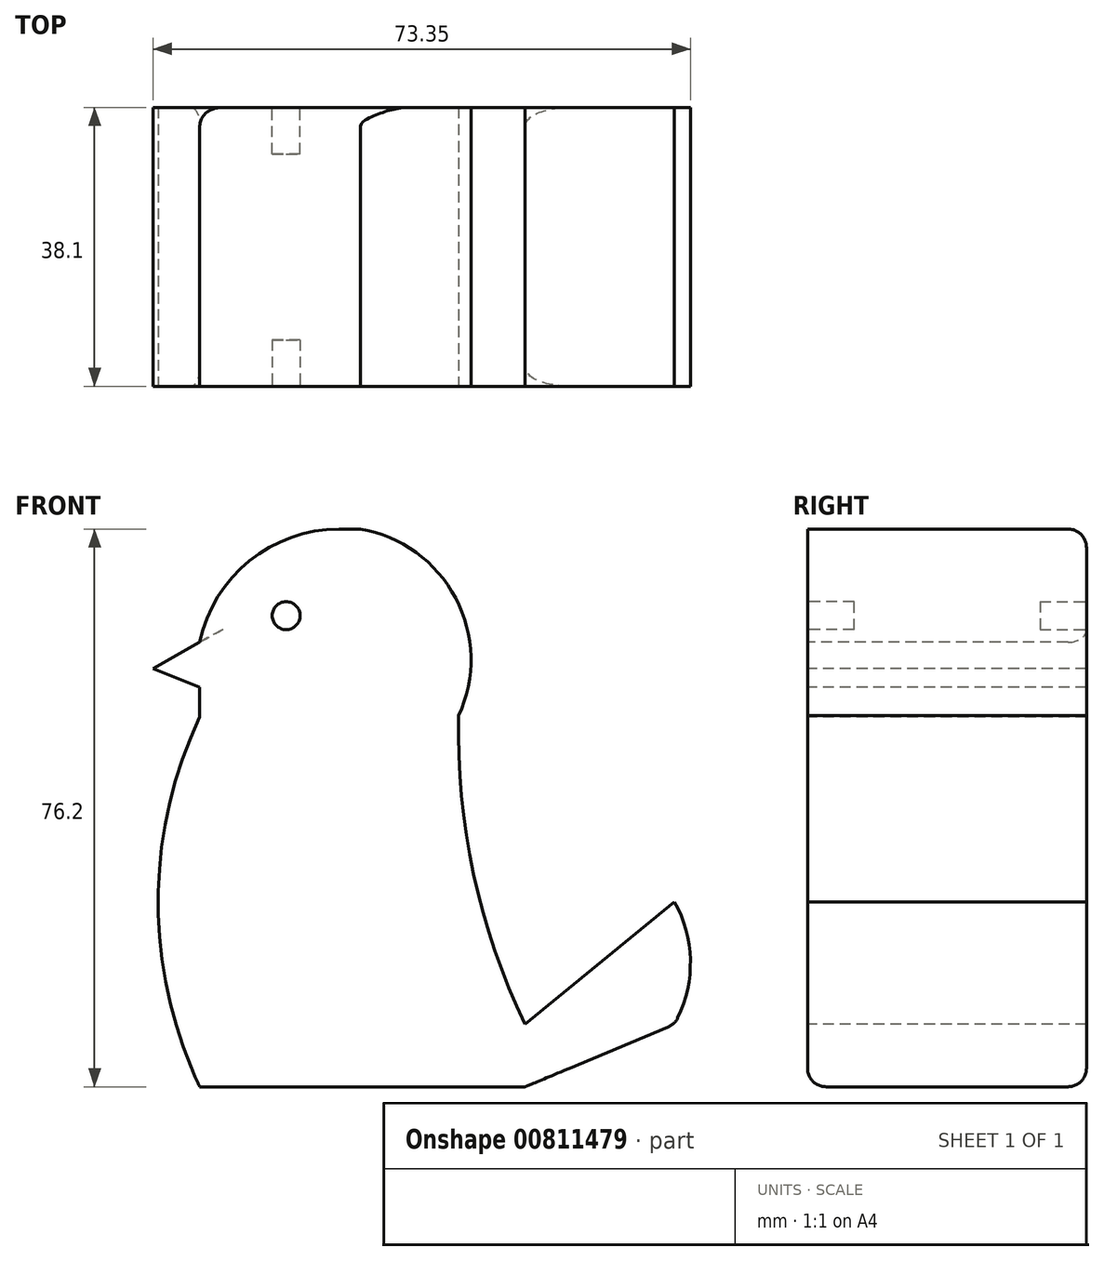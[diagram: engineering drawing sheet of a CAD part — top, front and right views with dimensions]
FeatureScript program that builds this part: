
annotation { "Feature Type Name" : "Feature", "Feature Type Description" : "" }
export const myFeature = defineFeature(function(context is Context, id is Id, definition is map)
    precondition{}
    {
        {
            var Q0;
            Q0=qCreatedBy(makeId("Front.planeOp"),FACE);
            var sketch = newSketch(context, id + "F0", { "sketchPlane" : qUnion([Q0])});
            skLineSegment(sketch, "E0", {"start": v(0, 0) * mm, "end": v(76.2, 0) * mm});
            skLineSegment(sketch, "E1", {"start": v(76.2, 0) * mm, "end": v(76.2, 76.2) * mm});
            skLineSegment(sketch, "E2", {"start": v(0, 76.2) * mm, "end": v(0, 0) * mm});
            skLineSegment(sketch, "E3", {"start": v(0, 76.2) * mm, "end": v(76.2, 76.2) * mm});
            skSolve(sketch);
        }
        {
            var Q0;
            Q0=makeQuery(id+"F0.imprint","IMPRINT",FACE,{"disambiguationData":[TD([[makeQuery(id+"F0.imprint","IMPRINT",EDGE,{"derivedFrom":sQuery(id+"F0.wireOp",EDGE,"E0")}),1.0]])]});
            extrude(context, id + "F1", {"entities" : qUnion([Q0]), "depth" : 38.1 * mm, "offsetDistance" : 25.4 * mm});
        }
        {
            var Q0;
            Q0=makeQuery(id+"F1.opExtrude","CAP_FACE",FACE,{"disambiguationData":[OSD([sQuery(id+"F0.wireOp",EDGE,"E0"),sQuery(id+"F0.wireOp",EDGE,"E1"),sQuery(id+"F0.wireOp",EDGE,"E2"),sQuery(id+"F0.wireOp",EDGE,"E3")])],"isStart":false});
            var sketch = newSketch(context, id + "F2", { "sketchPlane" : qUnion([Q0])});
            skLineSegment(sketch, "E4", {"start": v(0, 0) * mm, "end": v(6.35, 0) * mm, "construction": true});
            skLineSegment(sketch, "E5", {"start": v(6.35, 0) * mm, "end": v(6.35, 76.2) * mm, "construction": true});
            skLineSegment(sketch, "E6", {"start": v(0, 76.2) * mm, "end": v(0, 50.5) * mm, "construction": true});
            skLineSegment(sketch, "E7", {"start": v(0, 76.2) * mm, "end": v(0, 57.15) * mm, "construction": true});
            skLineSegment(sketch, "E8", {"start": v(0, 50.5) * mm, "end": v(6.35, 50.5) * mm, "construction": true});
            skArc(sketch, "E9", {"start": v(6.35, 50.5) * mm, "mid": v(0.66, 25.25) * mm, "end": v(6.35, 0) * mm});
            skLineSegment(sketch, "E10", {"start": v(6.35, 54.58) * mm, "end": v(0, 57.15) * mm});
            skLineSegment(sketch, "E11", {"start": v(0, 57.15) * mm, "end": v(6.35, 60.72) * mm});
            skLineSegment(sketch, "E12", {"start": v(6.35, 50.5) * mm, "end": v(6.35, 54.58) * mm});
            skLineSegment(sketch, "E13", {"start": v(0, 76.2) * mm, "end": v(19.05, 76.2) * mm, "construction": true});
            skLineSegment(sketch, "E14", {"start": v(0, 76.2) * mm, "end": v(25.4, 76.2) * mm, "construction": true});
            skArc(sketch, "E15", {"start": v(25.4, 76.2) * mm, "mid": v(13.13, 71.84) * mm, "end": v(6.35, 60.72) * mm});
            skLineSegment(sketch, "E16", {"start": v(0, 0) * mm, "end": v(0.66, 26) * mm, "construction": true});
            skPoint(sketch, "E16.endSnap0", {"position": v(0.66, 25.25) * mm});
            skLineSegment(sketch, "E17", {"start": v(0, 0) * mm, "end": v(0, 19.05) * mm, "construction": true});
            skLineSegment(sketch, "E18", {"start": v(0, 19.05) * mm, "end": v(76.2, 19.05) * mm, "construction": true});
            skSolve(sketch);
        }
        {
            var Q0;
            {var subQ0=sQuery(id+"F2.wireOp",EDGE,"E9");Q0=makeQuery(id+"F2.imprint","IMPRINT",FACE,{"disambiguationData":[TD([[makeQuery(id+"F2.imprint","IMPRINT",EDGE,{"derivedFrom":subQ0}),1.0]])]});}
            var sketch = newSketch(context, id + "F3", { "sketchPlane" : qUnion([Q0])});
            skLineSegment(sketch, "E19", {"start": v(0, 0) * mm, "end": v(50.8, 0) * mm, "construction": true});
            skLineSegment(sketch, "E20", {"start": v(50.8, 0) * mm, "end": v(71.17, 8.53) * mm, "construction": true});
            skLineSegment(sketch, "E21", {"start": v(71.17, 25.27) * mm, "end": v(50.8, 8.53) * mm, "construction": true});
            skArc(sketch, "E22", {"start": v(71.17, 8.53) * mm, "mid": v(73.35, 16.9) * mm, "end": v(71.17, 25.27) * mm});
            skLineSegment(sketch, "E23", {"start": v(6.05, 50.7) * mm, "end": v(77.37, 50.7) * mm, "construction": true});
            skArc(sketch, "E24", {"start": v(41.71, 50.7) * mm, "mid": v(40.7, 67.81) * mm, "end": v(25.9, 76.44) * mm});
            skArc(sketch, "E25", {"start": v(41.71, 50.7) * mm, "mid": v(43.74, 29.07) * mm, "end": v(50.8, 8.53) * mm});
            skLineSegment(sketch, "E26", {"start": v(64.72, 19.97) * mm, "end": v(71.17, 25.27) * mm});
            skLineSegment(sketch, "E27", {"start": v(71.17, 25.27) * mm, "end": v(50.8, 8.53) * mm});
            skLineSegment(sketch, "E28", {"start": v(50.8, 0) * mm, "end": v(71.17, 8.53) * mm});
            skSolve(sketch);
        }
        {
            var Q0;
            {var subQ3=sQuery(id+"F2.wireOp",EDGE,"E9");Q0=makeQuery(id+"F2.imprint","IMPRINT",FACE,{"disambiguationData":[TD([[makeQuery(id+"F2.imprint","IMPRINT",EDGE,{"derivedFrom":subQ3}),-1.0]])]});}
            var Q1;
            {var subQ0=sQuery(id+"F2.wireOp",EDGE,"E11");Q1=makeQuery(id+"F2.imprint","IMPRINT",FACE,{"disambiguationData":[TD([[makeQuery(id+"F2.imprint","IMPRINT",EDGE,{"derivedFrom":subQ0}),1.0]])]});}
            var Q2;
            {var subQ1=sQuery(id+"F3.wireOp",EDGE,"E22");Q2=makeQuery(id+"F3.imprint","IMPRINT",FACE,{"disambiguationData":[TD([[makeQuery(id+"F3.imprint","IMPRINT",EDGE,{"derivedFrom":subQ1}),-1.0]])]});}
            extrude(context, id + "F4", {"entities" : qUnion([Q0, Q1, Q2]), "operationType" : NewBodyOperationType.REMOVE, "endBound" : BoundingType.UP_TO_NEXT, "oppositeDirection" : true, "depth" : 25.4 * mm, "offsetDistance" : 25.4 * mm});
        }
        {
            var Q0;
            Q0=makeQuery(id+"F4.boolean.opBoolean","COPY",EDGE,{"derivedFrom":makeQuery(id+"F4.opExtrude","CAP_EDGE",EDGE,{"disambiguationData":[OSD([sQuery(id+"F2.wireOp",EDGE,"E9")])],"isStart":true})});
            var Q1;
            Q1=makeQuery(id+"F4.boolean.opBoolean","COPY",EDGE,{"derivedFrom":makeQuery(id+"F4.opExtrude","CAP_EDGE",EDGE,{"disambiguationData":[OSD([sQuery(id+"F2.wireOp",EDGE,"E15")])],"isStart":true})});
            var Q2;
            Q2=makeQuery(id+"F4.boolean.opBoolean","COPY",EDGE,{"derivedFrom":makeQuery(id+"F4.opExtrude","CAP_EDGE",EDGE,{"disambiguationData":[OSD([sQuery(id+"F2.wireOp",EDGE,"E11")])],"isStart":true})});
            var Q3;
            Q3=makeQuery(id+"F4.boolean.opBoolean","COPY",EDGE,{"derivedFrom":makeQuery(id+"F4.opExtrude","CAP_EDGE",EDGE,{"disambiguationData":[OSD([sQuery(id+"F2.wireOp",EDGE,"E10")])],"isStart":true})});
            var Q4;
            Q4=makeQuery(id+"F4.boolean.opBoolean","COPY",EDGE,{"derivedFrom":makeQuery(id+"F4.opExtrude","CAP_EDGE",EDGE,{"disambiguationData":[OSD([sQuery(id+"F2.wireOp",EDGE,"E12")])],"isStart":true})});
            var Q5;
            Q5=makeQuery(id+"F4.boolean.opBoolean","COPY",EDGE,{"derivedFrom":makeQuery(id+"F4.opExtrude","CAP_EDGE",EDGE,{"disambiguationData":[OSD([sQuery(id+"F3.wireOp",EDGE,"E25")])],"isStart":true})});
            var Q6;
            Q6=makeQuery(id+"F4.boolean.opBoolean","COPY",EDGE,{"derivedFrom":makeQuery(id+"F4.opExtrude","CAP_EDGE",EDGE,{"disambiguationData":[OSD([sQuery(id+"F3.wireOp",EDGE,"E24")])],"isStart":true})});
            var Q7;
            Q7=makeQuery(id+"F4.boolean.opBoolean","COPY",EDGE,{"derivedFrom":makeQuery(id+"F4.opExtrude","CAP_EDGE",EDGE,{"disambiguationData":[OSD([sQuery(id+"F3.wireOp",EDGE,"E27")])],"isStart":true})});
            var Q8;
            Q8=makeQuery(id+"F4.boolean.opBoolean","COPY",EDGE,{"derivedFrom":makeQuery(id+"F4.opExtrude","CAP_EDGE",EDGE,{"disambiguationData":[OSD([sQuery(id+"F3.wireOp",EDGE,"E22")])],"isStart":true})});
            var Q9;
            Q9=makeQuery(id+"F4.boolean.opBoolean","COPY",EDGE,{"derivedFrom":makeQuery(id+"F4.opExtrude","CAP_EDGE",EDGE,{"disambiguationData":[OSD([sQuery(id+"F3.wireOp",EDGE,"E28")])],"isStart":true})});
            var Q10;
            Q10=makeQuery(id+"F1.opExtrude","CAP_EDGE",EDGE,{"disambiguationData":[OSD([sQuery(id+"F0.wireOp",EDGE,"E0")])],"isStart":false});
            var Q11;
            Q11=makeQuery(id+"F4.boolean.opBoolean","COPY",EDGE,{"derivedFrom":makeQuery(id+"F4.opExtrude","CAP_EDGE",EDGE,{"disambiguationData":[OSD([sQuery(id+"F3.wireOp",EDGE,"E22")])],"isStart":false})});
            var Q12;
            Q12=makeQuery(id+"F4.boolean.opBoolean","COPY",EDGE,{"derivedFrom":makeQuery(id+"F4.opExtrude","CAP_EDGE",EDGE,{"disambiguationData":[OSD([sQuery(id+"F3.wireOp",EDGE,"E28")])],"isStart":false})});
            var Q13;
            Q13=makeQuery(id+"F4.boolean.opBoolean","COPY",EDGE,{"derivedFrom":makeQuery(id+"F4.opExtrude","CAP_EDGE",EDGE,{"disambiguationData":[OSD([sQuery(id+"F3.wireOp",EDGE,"E27")])],"isStart":false})});
            var Q14;
            Q14=makeQuery(id+"F4.boolean.opBoolean","COPY",EDGE,{"derivedFrom":makeQuery(id+"F4.opExtrude","CAP_EDGE",EDGE,{"disambiguationData":[OSD([sQuery(id+"F3.wireOp",EDGE,"E25")])],"isStart":false})});
            var Q15;
            Q15=makeQuery(id+"F1.opExtrude","CAP_EDGE",EDGE,{"disambiguationData":[OSD([sQuery(id+"F0.wireOp",EDGE,"E0")])],"isStart":true});
            var Q16;
            Q16=makeQuery(id+"F4.boolean.opBoolean","COPY",EDGE,{"derivedFrom":makeQuery(id+"F4.opExtrude","CAP_EDGE",EDGE,{"disambiguationData":[OSD([sQuery(id+"F2.wireOp",EDGE,"E9")])],"isStart":false})});
            var Q17;
            Q17=makeQuery(id+"F4.boolean.opBoolean","COPY",EDGE,{"derivedFrom":makeQuery(id+"F4.opExtrude","CAP_EDGE",EDGE,{"disambiguationData":[OSD([sQuery(id+"F2.wireOp",EDGE,"E12")])],"isStart":false})});
            var Q18;
            Q18=makeQuery(id+"F4.boolean.opBoolean","COPY",EDGE,{"derivedFrom":makeQuery(id+"F4.opExtrude","CAP_EDGE",EDGE,{"disambiguationData":[OSD([sQuery(id+"F2.wireOp",EDGE,"E10")])],"isStart":false})});
            var Q19;
            Q19=makeQuery(id+"F4.boolean.opBoolean","COPY",EDGE,{"derivedFrom":makeQuery(id+"F4.opExtrude","CAP_EDGE",EDGE,{"disambiguationData":[OSD([sQuery(id+"F2.wireOp",EDGE,"E11")])],"isStart":false})});
            var Q20;
            Q20=makeQuery(id+"F4.boolean.opBoolean","COPY",EDGE,{"derivedFrom":makeQuery(id+"F4.opExtrude","CAP_EDGE",EDGE,{"disambiguationData":[OSD([sQuery(id+"F2.wireOp",EDGE,"E15")])],"isStart":false})});
            var Q21;
            Q21=makeQuery(id+"F1.opExtrude","CAP_EDGE",EDGE,{"disambiguationData":[OSD([sQuery(id+"F0.wireOp",EDGE,"E3")])],"isStart":true});
            var Q22;
            Q22=makeQuery(id+"F4.boolean.opBoolean","COPY",EDGE,{"derivedFrom":makeQuery(id+"F4.opExtrude","CAP_EDGE",EDGE,{"disambiguationData":[OSD([sQuery(id+"F3.wireOp",EDGE,"E24")])],"isStart":false})});
            var Q23;
            Q23=makeQuery(id+"F4.boolean.opBoolean","COPY",EDGE,{"derivedFrom":makeQuery(id+"F4.opExtrude","SWEPT_EDGE",EDGE,{"disambiguationData":[OSD([sQuery(id+"F0.wireOp",EDGE,"E0"),sQuery(id+"F2.wireOp",EDGE,"E9")])]})});
            var Q24;
            Q24=makeQuery(id+"F4.boolean.opBoolean","COPY",EDGE,{"derivedFrom":makeQuery(id+"F4.opExtrude","SWEPT_EDGE",EDGE,{"disambiguationData":[OSD([sQuery(id+"F3.wireOp",EDGE,"E22"),sQuery(id+"F3.wireOp",EDGE,"E28")])]})});
            var Q25;
            Q25=makeQuery(id+"F4.boolean.opBoolean","COPY",EDGE,{"derivedFrom":makeQuery(id+"F4.opExtrude","SWEPT_EDGE",EDGE,{"disambiguationData":[OSD([sQuery(id+"F0.wireOp",EDGE,"E0"),sQuery(id+"F3.wireOp",EDGE,"E28")])]})});
            fillet(context, id + "F5", {"entities" : qUnion([Q0, Q1, Q2, Q3, Q4, Q5, Q6, Q7, Q8, Q9, Q10, Q11, Q12, Q13, Q14, Q15, Q16, Q17, Q18, Q19, Q20, Q21, Q22, Q23, Q24, Q25]), "radius" : 2.54 * mm, "tangentPropagation" : true, "allowEdgeOverflow" : false});
        }
        {
            var Q0;
            Q0=makeQuery(id+"F1.opExtrude","CAP_FACE",FACE,{"disambiguationData":[OSD([sQuery(id+"F0.wireOp",EDGE,"E0"),sQuery(id+"F0.wireOp",EDGE,"E1"),sQuery(id+"F0.wireOp",EDGE,"E2"),sQuery(id+"F0.wireOp",EDGE,"E3")])],"isStart":false});
            var sketch = newSketch(context, id + "F6", { "sketchPlane" : qUnion([Q0])});
            skLineSegment(sketch, "E29", {"start": v(10.3, 64.36) * mm, "end": v(40.79, 64.36) * mm, "construction": true});
            skCircle(sketch, "E30", {"center": v(18.15, 64.36) * mm, "radius": 1.9 * mm});
            skSolve(sketch);
        }
        {
            var Q0;
            Q0=makeQuery(id+"F6.imprint","IMPRINT",FACE,{"disambiguationData":[TD([[makeQuery(id+"F6.imprint","IMPRINT",EDGE,{"derivedFrom":sQuery(id+"F6.wireOp",EDGE,"E30")}),1.0]])]});
            var Q1;
            Q1=sQuery(id+"F6.wireOp",EDGE,"E30");
            extrude(context, id + "F7", {"entities" : qUnion([Q0]), "operationType" : NewBodyOperationType.REMOVE, "surfaceEntities" : qUnion([Q1]), "oppositeDirection" : true, "depth" : 6.35 * mm, "offsetDistance" : 25.4 * mm});
        }
        {
            var Q0;
            Q0=makeQuery(id+"F1.opExtrude","CAP_FACE",FACE,{"disambiguationData":[OSD([sQuery(id+"F0.wireOp",EDGE,"E0"),sQuery(id+"F0.wireOp",EDGE,"E1"),sQuery(id+"F0.wireOp",EDGE,"E2"),sQuery(id+"F0.wireOp",EDGE,"E3")])],"isStart":true});
            var sketch = newSketch(context, id + "F8", { "sketchPlane" : qUnion([Q0])});
            skSolve(sketch);
        }
        {
            var Q0;
            Q0=makeQuery(id+"F6.imprint","IMPRINT",FACE,{"disambiguationData":[TD([[makeQuery(id+"F6.imprint","IMPRINT",EDGE,{"derivedFrom":sQuery(id+"F6.wireOp",EDGE,"E30")}),1.0]])]});
            extrude(context, id + "F9", {"entities" : qUnion([Q0]), "operationType" : NewBodyOperationType.REMOVE, "oppositeDirection" : true, "depth" : 6.35 * mm, "offsetDistance" : 25.4 * mm});
        }
        {
            var Q0;
            {var subQ0=sQuery(id+"F0.wireOp",EDGE,"E3");var subQ1=sQuery(id+"F0.wireOp",EDGE,"E1");var subQ2=sQuery(id+"F0.wireOp",EDGE,"E0");var subQ3=makeQuery(id+"F1.opExtrude","CAP_FACE",FACE,{"disambiguationData":[OSD([subQ2,subQ1,sQuery(id+"F0.wireOp",EDGE,"E2"),subQ0])],"isStart":true});var subQ4=subQ3;Q0=makeQuery(id+"F8.imprint","IMPRINT",FACE,{"disambiguationData":[TD([[makeQuery(id+"F8.imprint","IMPRINT",EDGE,{"derivedFrom":makeQuery(id+"F5.opFillet","BLEND_EDGE",EDGE,{"blendedFrom":[makeQuery(id+"F1.opExtrude","CAP_EDGE",EDGE,{"disambiguationData":[OSD([subQ2])],"isStart":true}),subQ4],"blendedInto":[subQ4]})}),1.0]])]});}
            var sketch = newSketch(context, id + "F10", { "sketchPlane" : qUnion([Q0])});
            skCircle(sketch, "E31", {"center": v(-18.15, 64.38) * mm, "radius": 1.9 * mm});
            skSolve(sketch);
        }
        {
            var Q0;
            Q0 = qSketchRegion(id + "F10", true);
            extrude(context, id + "F11", {"entities" : qUnion([Q0]), "operationType" : NewBodyOperationType.REMOVE, "oppositeDirection" : true, "depth" : 6.35 * mm, "offsetDistance" : 25.4 * mm});
        }
    });
